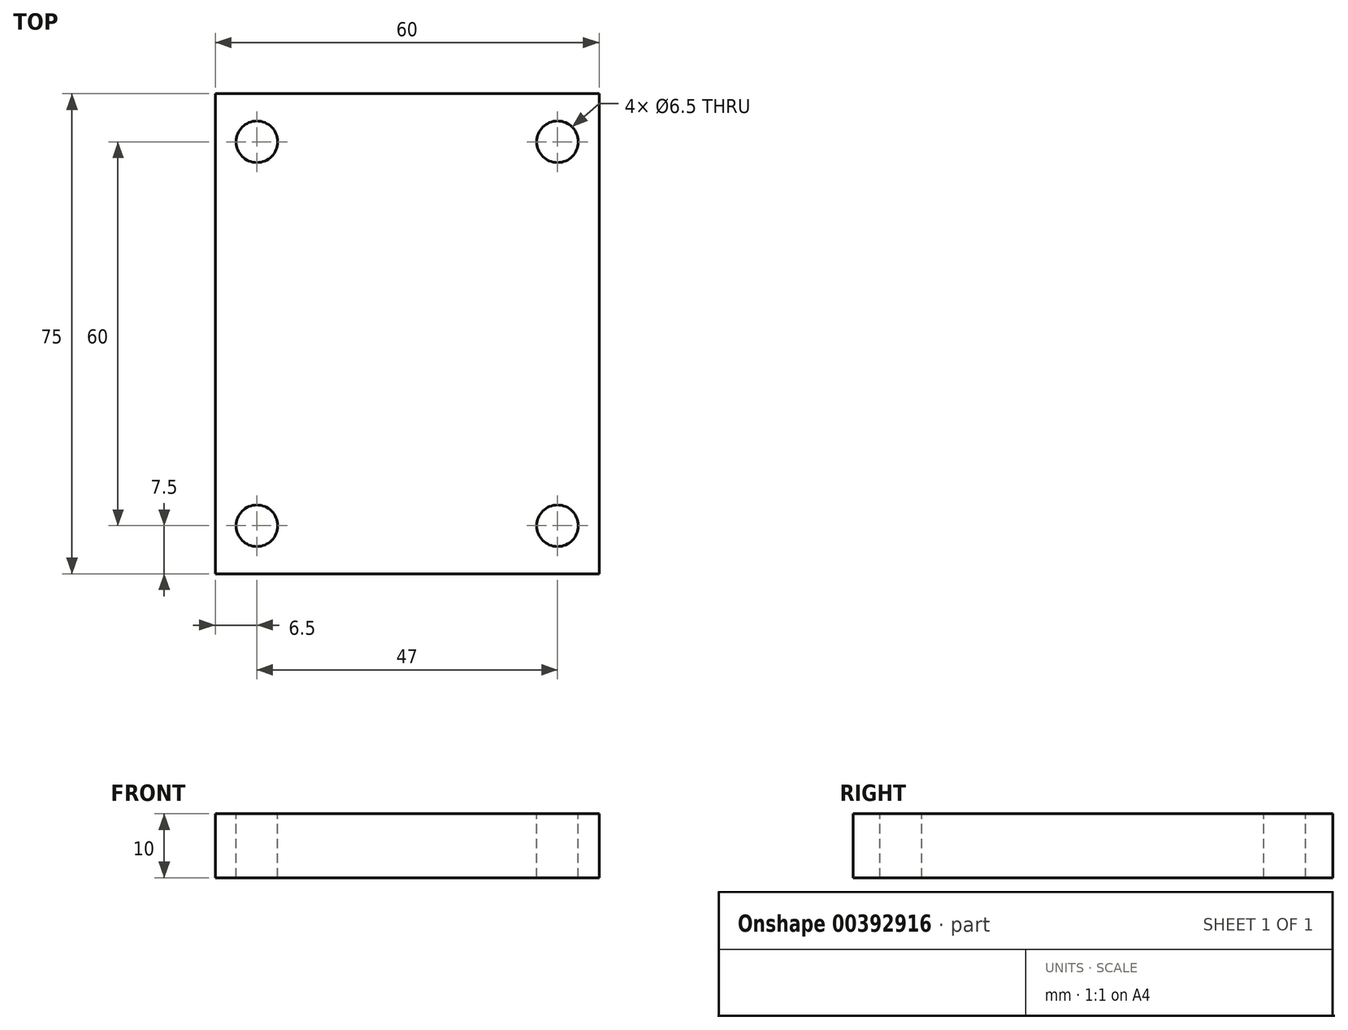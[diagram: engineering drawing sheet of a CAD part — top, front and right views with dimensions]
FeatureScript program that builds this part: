
annotation { "Feature Type Name" : "Feature", "Feature Type Description" : "" }
export const myFeature = defineFeature(function(context is Context, id is Id, definition is map)
    precondition{}
    {
        {
            var Q0;
            Q0=qCreatedBy(makeId("Top.planeOp"),FACE);
            var sketch = newSketch(context, id + "F0", { "sketchPlane" : qUnion([Q0])});
            skLineSegment(sketch, "E0.bottom", {"start": v(-30, 37.5) * mm, "end": v(30, 37.5) * mm});
            skLineSegment(sketch, "E0.top", {"start": v(-30, -37.5) * mm, "end": v(30, -37.5) * mm});
            skLineSegment(sketch, "E0.left", {"start": v(-30, 37.5) * mm, "end": v(-30, -37.5) * mm});
            skLineSegment(sketch, "E0.right", {"start": v(30, 37.5) * mm, "end": v(30, -37.5) * mm});
            skLineSegment(sketch, "E1", {"start": v(0, 76.83) * mm, "end": v(0, -62.83) * mm, "construction": true});
            skLineSegment(sketch, "E2", {"start": v(-62.67, 0) * mm, "end": v(69.33, 0) * mm, "construction": true});
            skLineSegment(sketch, "E3.bottom", {"start": v(-23.5, 30) * mm, "end": v(23.5, 30) * mm, "construction": true});
            skLineSegment(sketch, "E3.top", {"start": v(-23.5, -30) * mm, "end": v(23.5, -30) * mm, "construction": true});
            skLineSegment(sketch, "E3.left", {"start": v(-23.5, 30) * mm, "end": v(-23.5, -30) * mm, "construction": true});
            skLineSegment(sketch, "E3.right", {"start": v(23.5, 30) * mm, "end": v(23.5, -30) * mm, "construction": true});
            skSolve(sketch);
        }
        {
            var Q0;
            Q0=makeQuery(id+"F0.imprint","IMPRINT",FACE,{"disambiguationData":[TD([[makeQuery(id+"F0.imprint","IMPRINT",EDGE,{"derivedFrom":sQuery(id+"F0.wireOp",EDGE,"E0.bottom")}),-1.0]])]});
            extrude(context, id + "F1", {"entities" : qUnion([Q0]), "oppositeDirection" : true, "depth" : 10 * mm});
        }
        {
            var Q0;
            Q0=qCreatedBy(makeId("Top.planeOp"),FACE);
            var sketch = newSketch(context, id + "F2", { "sketchPlane" : qUnion([Q0])});
            skCircle(sketch, "E4", {"center": v(-23.5, 30) * mm, "radius": 3.25 * mm});
            skCircle(sketch, "E5.MirrorC", {"center": v(23.5, 30) * mm, "radius": 3.25 * mm});
            skCircle(sketch, "E6.MirrorC", {"center": v(-23.5, -30) * mm, "radius": 3.25 * mm});
            skCircle(sketch, "E7.MirrorC", {"center": v(23.5, -30) * mm, "radius": 3.25 * mm});
            skSolve(sketch);
        }
        {
            var Q0;
            Q0 = qSketchRegion(id + "F2", true);
            extrude(context, id + "F3", {"entities" : qUnion([Q0]), "operationType" : NewBodyOperationType.REMOVE, "endBound" : BoundingType.THROUGH_ALL, "oppositeDirection" : true, "depth" : 25.4 * mm});
        }
    });
